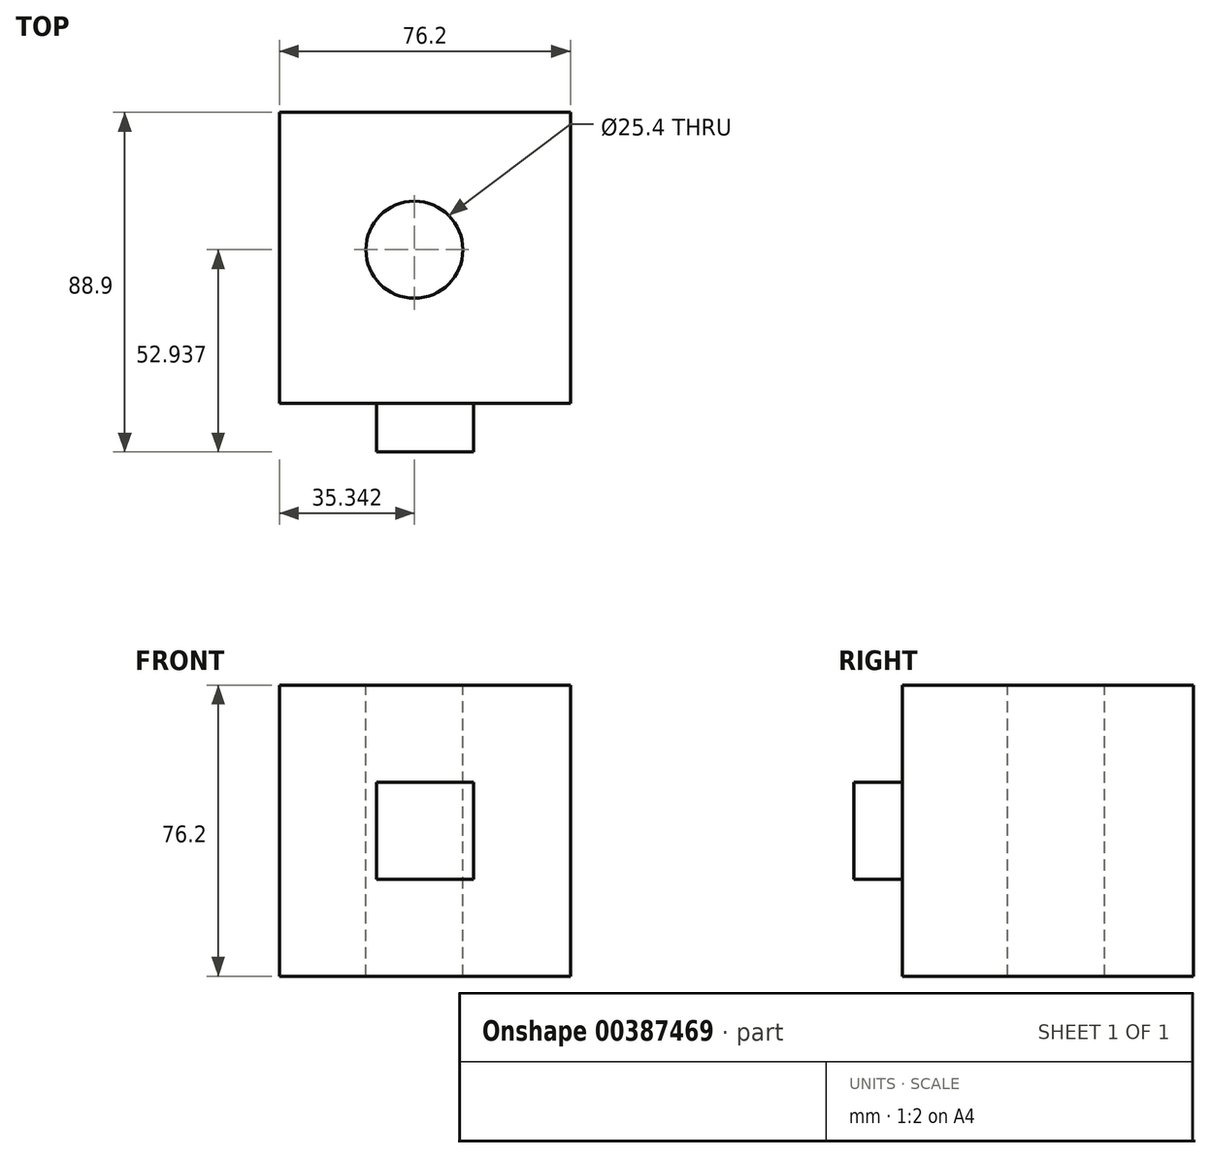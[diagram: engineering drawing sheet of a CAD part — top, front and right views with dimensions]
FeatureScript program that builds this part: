
annotation { "Feature Type Name" : "Feature", "Feature Type Description" : "" }
export const myFeature = defineFeature(function(context is Context, id is Id, definition is map)
    precondition{}
    {
        {
            var Q0;
            Q0=qCreatedBy(makeId("Front.planeOp"),FACE);
            var sketch = newSketch(context, id + "F0", { "sketchPlane" : qUnion([Q0])});
            skLineSegment(sketch, "E0.bottom", {"start": v(34.43, 13.14) * mm, "end": v(-41.77, 13.14) * mm});
            skLineSegment(sketch, "E0.top", {"start": v(34.43, 89.34) * mm, "end": v(-41.77, 89.34) * mm});
            skLineSegment(sketch, "E0.left", {"start": v(34.43, 13.14) * mm, "end": v(34.43, 89.34) * mm});
            skLineSegment(sketch, "E0.right", {"start": v(-41.77, 13.14) * mm, "end": v(-41.77, 89.34) * mm});
            skLineSegment(sketch, "E1.bottom", {"start": v(-52.2, 0) * mm, "end": v(-128.4, 0) * mm});
            skLineSegment(sketch, "E1.top", {"start": v(-52.2, 76.2) * mm, "end": v(-128.4, 76.2) * mm});
            skLineSegment(sketch, "E1.left", {"start": v(-52.2, 0) * mm, "end": v(-52.2, 76.2) * mm});
            skLineSegment(sketch, "E1.right", {"start": v(-128.4, 0) * mm, "end": v(-128.4, 76.2) * mm});
            skSolve(sketch);
        }
        {
            var Q0;
            Q0=makeQuery(id+"F0.imprint","IMPRINT",FACE,{"disambiguationData":[TD([[makeQuery(id+"F0.imprint","IMPRINT",EDGE,{"derivedFrom":sQuery(id+"F0.wireOp",EDGE,"E1.bottom")}),-1.0]])]});
            extrude(context, id + "F1", {"entities" : qUnion([Q0]), "depth" : 76.2 * mm});
        }
        {
            var Q0;
            Q0=makeQuery(id+"F1.opExtrude","SWEPT_FACE",FACE,{"disambiguationData":[OSD([sQuery(id+"F0.wireOp",EDGE,"E1.top")])]});
            var sketch = newSketch(context, id + "F2", { "sketchPlane" : qUnion([Q0])});
            skPoint(sketch, "E2", {"position": v(-93.06, -35.96) * mm});
            skSolve(sketch);
        }
        {
            var Q0;
            Q0=sQuery(id+"F2.wireOp",VERTEX,"E2");
            var Q1;
            Q1=makeQuery(id+"F1.opExtrude","SWEPT_BODY",BODY,{"disambiguationData":[OSD([sQuery(id+"F0.wireOp",EDGE,"E1.bottom"),sQuery(id+"F0.wireOp",EDGE,"E1.top"),sQuery(id+"F0.wireOp",EDGE,"E1.left"),sQuery(id+"F0.wireOp",EDGE,"E1.right")])]});
            hole(context, id + "F3", {"style" : HoleStyle.SIMPLE, "endStyle" : HoleEndStyle.THROUGH, "holeDiameter" : 25.4 * mm, "isTappedThrough" : true, "tappedDepth" : 12.7 * mm, "tapClearance" : 3, "locations" : qUnion([Q0]), "scope" : qUnion([Q1])});
        }
        {
            var Q0;
            Q0=makeQuery(id+"F1.opExtrude","CAP_FACE",FACE,{"disambiguationData":[OSD([sQuery(id+"F0.wireOp",EDGE,"E1.bottom"),sQuery(id+"F0.wireOp",EDGE,"E1.top"),sQuery(id+"F0.wireOp",EDGE,"E1.left"),sQuery(id+"F0.wireOp",EDGE,"E1.right")])],"isStart":false});
            var sketch = newSketch(context, id + "F4", { "sketchPlane" : qUnion([Q0])});
            skLineSegment(sketch, "E3.bottom", {"start": v(-103, 50.8) * mm, "end": v(-77.6, 50.8) * mm});
            skLineSegment(sketch, "E3.top", {"start": v(-103, 25.4) * mm, "end": v(-77.6, 25.4) * mm});
            skLineSegment(sketch, "E3.left", {"start": v(-103, 50.8) * mm, "end": v(-103, 25.4) * mm});
            skLineSegment(sketch, "E3.right", {"start": v(-77.6, 50.8) * mm, "end": v(-77.6, 25.4) * mm});
            skPoint(sketch, "E3.middle", {"position": v(-90.3, 38.1) * mm});
            skPoint(sketch, "E3.middle.positionSnap0", {"position": v(-52.2, 38.1) * mm});
            skPoint(sketch, "E3.middle.positionSnap1", {"position": v(-90.3, 76.2) * mm});
            skPoint(sketch, "E3.centerSnap0", {"position": v(-52.2, 38.1) * mm});
            skPoint(sketch, "E3.centerSnap1", {"position": v(-90.3, 76.2) * mm});
            skSolve(sketch);
        }
        {
            var Q0;
            Q0=makeQuery(id+"F4.imprint","IMPRINT",FACE,{"disambiguationData":[TD([[makeQuery(id+"F4.imprint","IMPRINT",EDGE,{"derivedFrom":sQuery(id+"F4.wireOp",EDGE,"E3.bottom")}),-1.0]])]});
            extrude(context, id + "F5", {"entities" : qUnion([Q0]), "operationType" : NewBodyOperationType.ADD, "depth" : 12.7 * mm});
        }
    });
